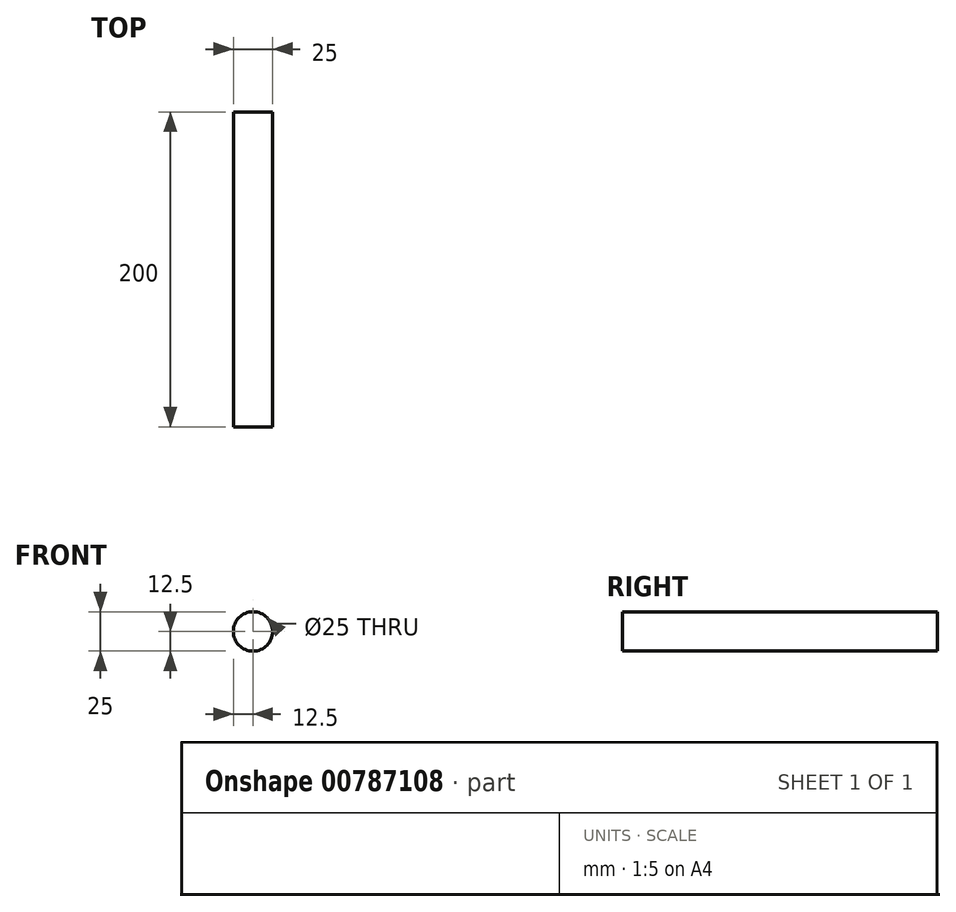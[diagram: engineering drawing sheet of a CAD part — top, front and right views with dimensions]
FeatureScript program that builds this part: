
annotation { "Feature Type Name" : "Feature", "Feature Type Description" : "" }
export const myFeature = defineFeature(function(context is Context, id is Id, definition is map)
    precondition{}
    {
        {
            var Q0;
            Q0=qCreatedBy(makeId("Front.planeOp"),FACE);
            var sketch = newSketch(context, id + "F0", { "sketchPlane" : qUnion([Q0])});
            skCircle(sketch, "E0", {"center": v(0, 0) * mm, "radius": 12.5 * mm});
            skSolve(sketch);
        }
        {
            var Q0;
            Q0=sQuery(id+"F0.wireOp",EDGE,"E0");
            extrude(context, id + "F1", {"bodyType" : ToolBodyType.SURFACE, "surfaceEntities" : qUnion([Q0]), "oppositeDirection" : true, "depth" : 200 * mm, "offsetDistance" : 25 * mm});
        }
    });
